# Revit family: Magnuson-Cantha-Coat_Hook-
name_source: partatom
category: Furniture
units: mm (PartAtom-declared; Revit-internal decimal feet)

## family parameters
Cut with Voids When Loaded = No
Host = Face
Room Calculation Point = No
Shared = No

## types (8) — shared parameters
Assembly Code = E2020200
Default Elevation = 48"
Keynote = 12500
Manufacturer = Magnuson Group
Plate Finish = MAG - Coated Steel Satin Black
Post Finish = MAG - Coated Steel Satin Black
Revit File Built By = https://servex-us.com
Type Comments = Cantha
URL = www.magnusongroup.com

## per-type parameters (varying)
| type | Description | Front Finish | H Post | Hook-L | Hook-M | Hook-S | Hook-XL |
| CANTHA-S | Cantha Coat Hook - S | MAG - Coated Steel Satin Black | 1 7/64" | No | No | Yes | No |
| CANTHA-SW | Cantha Coat Hook with Oak Veneer  Front Plate - S | MAG - Matt Oak Ply wood | 1 7/64" | No | No | Yes | No |
| CANTHA-M | Cantha Coat Hook - M | MAG - Coated Steel Satin Black | 1 7/64" | No | Yes | No | No |
| CANTHA-MW | Cantha Coat Hook with Oak Veneer  Front Plate - M | MAG - Matt Oak Ply wood | 1 7/64" | No | Yes | No | No |
| CANTHA-L | Cantha Coat Hook - L | MAG - Coated Steel Satin Black | 1 1/2" | Yes | No | No | No |
| CANTHA-LW | Cantha Coat Hook with Oak Veneer Front Plate - L | MAG - Matt Oak Ply wood | 1 1/2" | Yes | No | No | No |
| CANTHA-XL | Cantha Coat Hook - XL | MAG - Coated Steel Satin Black | 1 1/2" | No | No | No | Yes |
| CANTHA-XLW | Cantha Coat Hook with Oak Veneer Front Plate - XL | MAG - Matt Oak Ply wood | 1 1/2" | No | No | No | Yes |

note: column(s) folded — value = type name in every type: Model

## geometry (parser evidence)
native form markers: Sweep x4
no freeform markers — native parametric forms only
